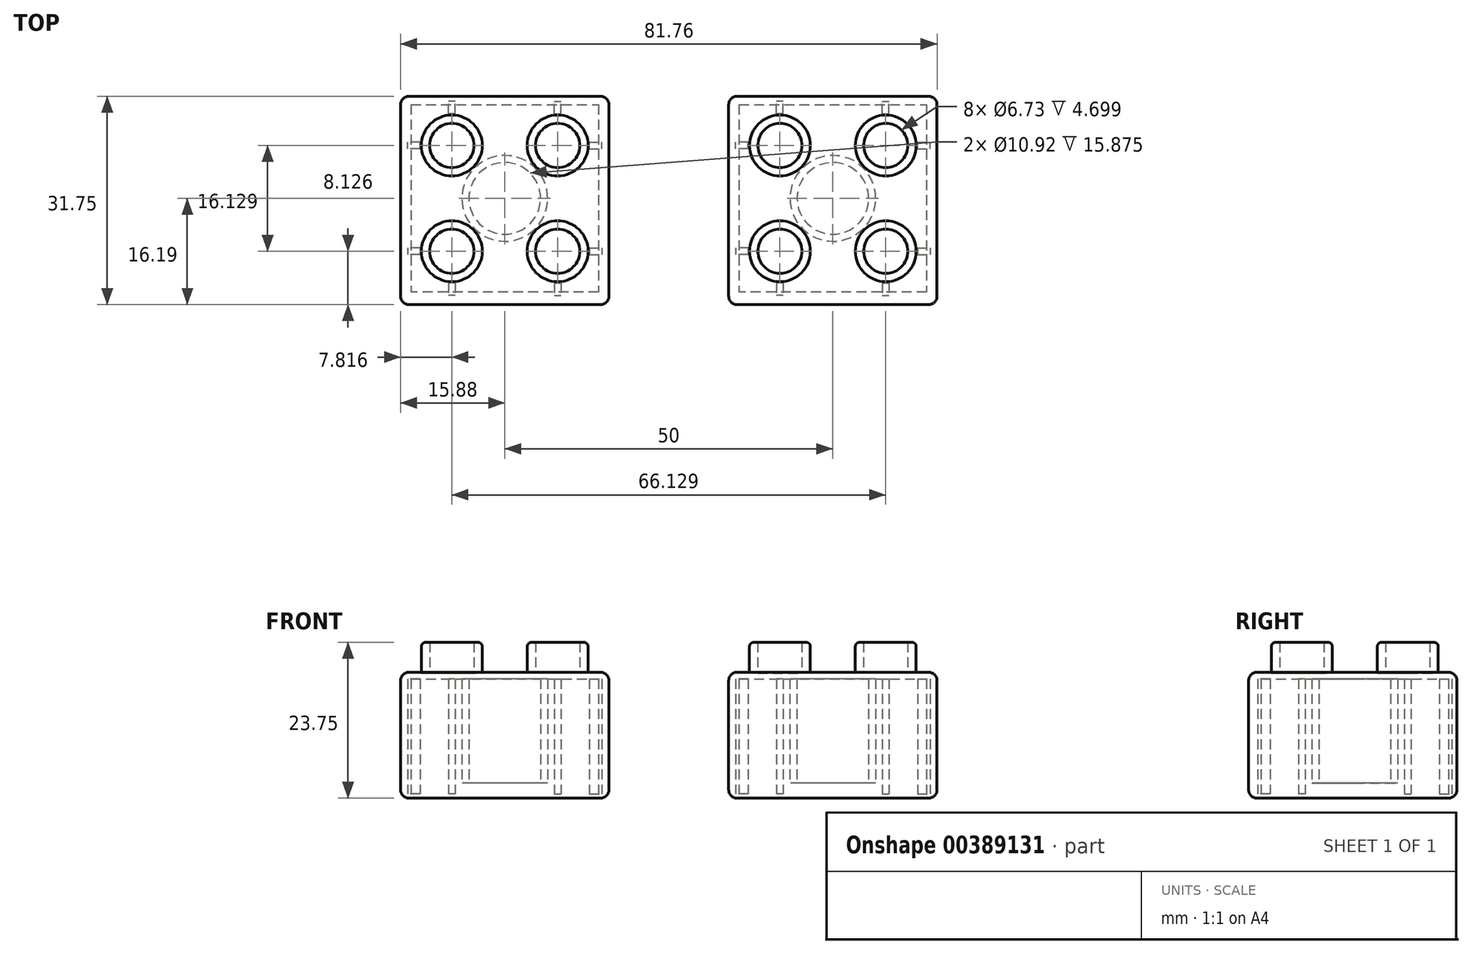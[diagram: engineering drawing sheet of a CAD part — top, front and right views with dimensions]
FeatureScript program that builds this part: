
annotation { "Feature Type Name" : "Feature", "Feature Type Description" : "" }
export const myFeature = defineFeature(function(context is Context, id is Id, definition is map)
    precondition{}
    {
        {
            var Q0;
            Q0=qCreatedBy(makeId("Top.planeOp"),FACE);
            var sketch = newSketch(context, id + "F0", { "sketchPlane" : qUnion([Q0])});
            skPoint(sketch, "E0", {"position": v(0, 16.87) * mm});
            skPoint(sketch, "E1", {"position": v(0, 15.88) * mm});
            skPoint(sketch, "E2", {"position": v(0, -14.88) * mm});
            skPoint(sketch, "E3", {"position": v(0, -15.88) * mm});
            skPoint(sketch, "E4", {"position": v(17.1, 0) * mm});
            skPoint(sketch, "E5", {"position": v(15.88, 0) * mm});
            skPoint(sketch, "E6", {"position": v(-15.88, 0) * mm});
            skPoint(sketch, "E7", {"position": v(15.64, 15.88) * mm});
            skPoint(sketch, "E8", {"position": v(15.88, 15.56) * mm});
            skPoint(sketch, "E9", {"position": v(-16.3, -15.88) * mm});
            skPoint(sketch, "E10", {"position": v(-15.88, -16.2) * mm});
            skLineSegment(sketch, "E11.bottom", {"start": v(-15.88, -16.2) * mm, "end": v(15.88, -16.2) * mm});
            skLineSegment(sketch, "E11.top", {"start": v(-15.88, 15.56) * mm, "end": v(15.88, 15.56) * mm});
            skLineSegment(sketch, "E11.left", {"start": v(-15.88, -16.2) * mm, "end": v(-15.88, 15.56) * mm});
            skLineSegment(sketch, "E11.right", {"start": v(15.88, -16.2) * mm, "end": v(15.88, 15.56) * mm});
            skSolve(sketch);
        }
        {
            var Q0;
            Q0=makeQuery(id+"F0.imprint","IMPRINT",FACE,{"disambiguationData":[TD([[makeQuery(id+"F0.imprint","IMPRINT",EDGE,{"derivedFrom":sQuery(id+"F0.wireOp",EDGE,"E11.bottom")}),1.0]])]});
            var sketch = newSketch(context, id + "F1", { "sketchPlane" : qUnion([Q0])});
            skPoint(sketch, "E12", {"position": v(14.77, 0) * mm});
            skPoint(sketch, "E13", {"position": v(14.29, 0) * mm});
            skPoint(sketch, "E14", {"position": v(-14.29, 0) * mm});
            skPoint(sketch, "E15", {"position": v(-14.29, -14.92) * mm});
            skPoint(sketch, "E16", {"position": v(-14.29, -14.29) * mm});
            skPoint(sketch, "E17", {"position": v(14.29, 14.33) * mm});
            skPoint(sketch, "E18", {"position": v(14.29, 14.29) * mm});
            skLineSegment(sketch, "E19.bottom", {"start": v(-14.29, -14.29) * mm, "end": v(14.29, -14.29) * mm});
            skLineSegment(sketch, "E19.top", {"start": v(-14.29, 14.29) * mm, "end": v(14.29, 14.29) * mm});
            skLineSegment(sketch, "E19.left", {"start": v(-14.29, -14.29) * mm, "end": v(-14.29, 14.29) * mm});
            skLineSegment(sketch, "E19.right", {"start": v(14.29, -14.29) * mm, "end": v(14.29, 14.29) * mm});
            skSolve(sketch);
        }
        {
            var Q0;
            Q0=makeQuery(id+"F1.imprint","IMPRINT",FACE,{"disambiguationData":[TD([[makeQuery(id+"F1.imprint","IMPRINT",EDGE,{"derivedFrom":sQuery(id+"F1.wireOp",EDGE,"E19.bottom")}),1.0]])]});
            var sketch = newSketch(context, id + "F2", { "sketchPlane" : qUnion([Q0])});
            skPoint(sketch, "E20", {"position": v(0, 0) * mm});
            skCircle(sketch, "E21", {"center": v(0, 0) * mm, "radius": 6.54 * mm});
            skSolve(sketch);
        }
        {
            var Q0;
            Q0=makeQuery(id+"F1.imprint","IMPRINT",FACE,{"disambiguationData":[TD([[makeQuery(id+"F1.imprint","IMPRINT",EDGE,{"derivedFrom":sQuery(id+"F1.wireOp",EDGE,"E19.bottom")}),1.0]])]});
            var sketch = newSketch(context, id + "F3", { "sketchPlane" : qUnion([Q0])});
            skPoint(sketch, "E22", {"position": v(0, 0) * mm});
            skCircle(sketch, "E23", {"center": v(0, 0) * mm, "radius": 5.46 * mm});
            skSolve(sketch);
        }
        {
            var Q0;
            Q0=makeQuery(id+"F1.imprint","IMPRINT",FACE,{"disambiguationData":[TD([[makeQuery(id+"F1.imprint","IMPRINT",EDGE,{"derivedFrom":sQuery(id+"F1.wireOp",EDGE,"E19.bottom")}),1.0]])]});
            var sketch = newSketch(context, id + "F4", { "sketchPlane" : qUnion([Q0])});
            skPoint(sketch, "E24", {"position": v(0, 1.02) * mm});
            skPoint(sketch, "E25", {"position": v(0, 0.95) * mm});
            skPoint(sketch, "E26", {"position": v(0, -0.95) * mm});
            skPoint(sketch, "E27", {"position": v(-0.23, 0) * mm});
            skPoint(sketch, "E28", {"position": v(-0.5, 0) * mm});
            skPoint(sketch, "E29", {"position": v(0.3, 0) * mm});
            skPoint(sketch, "E30", {"position": v(0.5, 0) * mm});
            skPoint(sketch, "E31", {"position": v(-0.5, -0.86) * mm});
            skPoint(sketch, "E32", {"position": v(-0.5, -0.95) * mm});
            skPoint(sketch, "E33", {"position": v(0.5, 0.95) * mm});
            skLineSegment(sketch, "E34.bottom", {"start": v(-0.5, -0.95) * mm, "end": v(0.5, -0.95) * mm});
            skLineSegment(sketch, "E34.top", {"start": v(-0.5, 0.95) * mm, "end": v(0.5, 0.95) * mm});
            skLineSegment(sketch, "E34.left", {"start": v(-0.5, -0.95) * mm, "end": v(-0.5, 0.95) * mm});
            skLineSegment(sketch, "E34.right", {"start": v(0.5, -0.95) * mm, "end": v(0.5, 0.95) * mm});
            skSolve(sketch);
        }
        {
            var Q0;
            Q0=qSketchRegion(id+"F0",true);
            extrude(context, id + "F5", {"entities" : qUnion([Q0]), "depth" : 19.18 * mm});
        }
        {
            var Q0;
            Q0=qSketchRegion(id+"F1",true);
            extrude(context, id + "F6", {"entities" : qUnion([Q0]), "operationType" : NewBodyOperationType.REMOVE, "depth" : 18.16 * mm, "hasSecondDirection" : true, "secondDirectionOppositeDirection" : true, "secondDirectionDepth" : 0.38 * mm});
        }
        {
            var Q0;
            Q0=qSketchRegion(id+"F2",true);
            extrude(context, id + "F7", {"entities" : qUnion([Q0]), "operationType" : NewBodyOperationType.ADD, "depth" : 15.88 * mm});
        }
        {
            var Q0;
            Q0=qSketchRegion(id+"F3",true);
            extrude(context, id + "F8", {"entities" : qUnion([Q0]), "operationType" : NewBodyOperationType.REMOVE, "depth" : 15.88 * mm, "hasSecondDirection" : true, "secondDirectionOppositeDirection" : true, "secondDirectionDepth" : 0.64 * mm});
        }
        {
            var Q0;
            Q0=makeQuery(id+"F7.opExtrude","SWEPT_BODY",BODY,{"disambiguationData":[OSD([sQuery(id+"F2.wireOp",EDGE,"E21")])]});
            transform(context, id + "F9", {"entities" : qUnion([Q0]), "transformType" : TransformType.TRANSLATION_3D, "dx" : 0 * mm, "dy" : 0 * mm, "dz" : 2.3 * mm, "makeCopy" : false});
        }
        {
            var Q0;
            Q0=makeQuery(id+"F4.imprint","IMPRINT",FACE,{"disambiguationData":[TD([[makeQuery(id+"F4.imprint","IMPRINT",EDGE,{"derivedFrom":sQuery(id+"F4.wireOp",EDGE,"E34.bottom")}),1.0]])]});
            extrude(context, id + "F10", {"entities" : qUnion([Q0]), "operationType" : NewBodyOperationType.ADD, "depth" : 17.53 * mm});
        }
        {
            var Q0;
            Q0=makeQuery(id+"F10.opExtrude","SWEPT_BODY",BODY,{"disambiguationData":[OSD([sQuery(id+"F4.wireOp",EDGE,"E34.bottom"),sQuery(id+"F4.wireOp",EDGE,"E34.top"),sQuery(id+"F4.wireOp",EDGE,"E34.left"),sQuery(id+"F4.wireOp",EDGE,"E34.right")])]});
            transform(context, id + "F11", {"entities" : qUnion([Q0]), "transformType" : TransformType.TRANSLATION_3D, "dx" : 8.06 * mm, "dy" : 13.86 * mm, "dz" : 0.64 * mm, "makeCopy" : false});
        }
        {
            var Q0;
            Q0=makeQuery(id+"F10.opExtrude","SWEPT_BODY",BODY,{"disambiguationData":[OSD([sQuery(id+"F4.wireOp",EDGE,"E34.bottom"),sQuery(id+"F4.wireOp",EDGE,"E34.top"),sQuery(id+"F4.wireOp",EDGE,"E34.left"),sQuery(id+"F4.wireOp",EDGE,"E34.right")])]});
            var Q1;
            Q1=qCreatedBy(makeId("Front.planeOp"),FACE);
            mirror(context, id + "F12", {"entities" : qUnion([Q0]), "mirrorPlane" : qUnion([Q1])});
        }
        {
            var Q0;
            Q0=makeQuery(id+"F12.opPattern","COPY",BODY,{"derivedFrom":makeQuery(id+"F10.opExtrude","SWEPT_BODY",BODY,{"disambiguationData":[OSD([sQuery(id+"F4.wireOp",EDGE,"E34.bottom"),sQuery(id+"F4.wireOp",EDGE,"E34.top"),sQuery(id+"F4.wireOp",EDGE,"E34.left"),sQuery(id+"F4.wireOp",EDGE,"E34.right")])]}),"instanceName":"1"});
            var Q1;
            Q1=makeQuery(id+"F10.opExtrude","SWEPT_BODY",BODY,{"disambiguationData":[OSD([sQuery(id+"F4.wireOp",EDGE,"E34.bottom"),sQuery(id+"F4.wireOp",EDGE,"E34.top"),sQuery(id+"F4.wireOp",EDGE,"E34.left"),sQuery(id+"F4.wireOp",EDGE,"E34.right")])]});
            var Q2;
            Q2=qCreatedBy(makeId("Right.planeOp"),FACE);
            mirror(context, id + "F13", {"entities" : qUnion([Q0, Q1]), "mirrorPlane" : qUnion([Q2])});
        }
        {
            var Q0;
            Q0=qCreatedBy(makeId("Front.planeOp"),FACE);
            var sketch = newSketch(context, id + "F14", { "sketchPlane" : qUnion([Q0])});
            skLineSegment(sketch, "E35", {"start": v(0, 40.9) * mm, "end": v(0, -32.36) * mm});
            skSolve(sketch);
        }
        {
            var Q0;
            Q0=makeQuery(id+"F12.opPattern","COPY",BODY,{"derivedFrom":makeQuery(id+"F10.opExtrude","SWEPT_BODY",BODY,{"disambiguationData":[OSD([sQuery(id+"F4.wireOp",EDGE,"E34.bottom"),sQuery(id+"F4.wireOp",EDGE,"E34.top"),sQuery(id+"F4.wireOp",EDGE,"E34.left"),sQuery(id+"F4.wireOp",EDGE,"E34.right")])]}),"instanceName":"1"});
            var Q1;
            Q1=makeQuery(id+"F13.opPattern","COPY",BODY,{"derivedFrom":makeQuery(id+"F12.opPattern","COPY",BODY,{"derivedFrom":makeQuery(id+"F10.opExtrude","SWEPT_BODY",BODY,{"disambiguationData":[OSD([sQuery(id+"F4.wireOp",EDGE,"E34.bottom"),sQuery(id+"F4.wireOp",EDGE,"E34.top"),sQuery(id+"F4.wireOp",EDGE,"E34.left"),sQuery(id+"F4.wireOp",EDGE,"E34.right")])]}),"instanceName":"1"}),"instanceName":"1"});
            var Q2;
            Q2=makeQuery(id+"F10.opExtrude","SWEPT_BODY",BODY,{"disambiguationData":[OSD([sQuery(id+"F4.wireOp",EDGE,"E34.bottom"),sQuery(id+"F4.wireOp",EDGE,"E34.top"),sQuery(id+"F4.wireOp",EDGE,"E34.left"),sQuery(id+"F4.wireOp",EDGE,"E34.right")])]});
            var Q3;
            Q3=makeQuery(id+"F13.opPattern","COPY",BODY,{"derivedFrom":makeQuery(id+"F10.opExtrude","SWEPT_BODY",BODY,{"disambiguationData":[OSD([sQuery(id+"F4.wireOp",EDGE,"E34.bottom"),sQuery(id+"F4.wireOp",EDGE,"E34.top"),sQuery(id+"F4.wireOp",EDGE,"E34.left"),sQuery(id+"F4.wireOp",EDGE,"E34.right")])]}),"instanceName":"1"});
            var Q4;
            Q4=sQuery(id+"F14.wireOp",EDGE,"E35");
            transform(context, id + "F15", {"entities" : qUnion([Q0, Q1, Q2, Q3]), "transformType" : TransformType.ROTATION, "transformAxis" : qUnion([Q4]), "angle" : 90 * degree, "makeCopy" : true});
        }
        {
            var Q0;
            Q0=qCreatedBy(makeId("Top.planeOp"),FACE);
            var sketch = newSketch(context, id + "F16", { "sketchPlane" : qUnion([Q0])});
            skCircle(sketch, "E36", {"center": v(0, 0) * mm, "radius": 4.64 * mm});
            skSolve(sketch);
        }
        {
            var Q0;
            Q0=qCreatedBy(makeId("Top.planeOp"),FACE);
            var sketch = newSketch(context, id + "F17", { "sketchPlane" : qUnion([Q0])});
            skCircle(sketch, "E37", {"center": v(0, 0) * mm, "radius": 3.37 * mm});
            skSolve(sketch);
        }
        {
            var Q0;
            Q0=makeQuery(id+"F16.imprint","IMPRINT",FACE,{"disambiguationData":[TD([[makeQuery(id+"F16.imprint","IMPRINT",EDGE,{"derivedFrom":sQuery(id+"F16.wireOp",EDGE,"E36")}),1.0]])]});
            extrude(context, id + "F18", {"entities" : qUnion([Q0]), "depth" : 4.7 * mm});
        }
        {
            var Q0;
            Q0=makeQuery(id+"F17.imprint","IMPRINT",FACE,{"disambiguationData":[TD([[makeQuery(id+"F17.imprint","IMPRINT",EDGE,{"derivedFrom":sQuery(id+"F17.wireOp",EDGE,"E37")}),1.0]])]});
            extrude(context, id + "F19", {"entities" : qUnion([Q0]), "operationType" : NewBodyOperationType.REMOVE, "depth" : 4.7 * mm});
        }
        {
            var Q0;
            Q0=makeQuery(id+"F18.opExtrude","SWEPT_BODY",BODY,{"disambiguationData":[OSD([sQuery(id+"F16.wireOp",EDGE,"E36")])]});
            transform(context, id + "F20", {"entities" : qUnion([Q0]), "transformType" : TransformType.TRANSLATION_3D, "dx" : 8.06 * mm, "dy" : 8.06 * mm, "dz" : 19.05 * mm, "makeCopy" : false});
        }
        {
            var Q0;
            Q0=makeQuery(id+"F18.opExtrude","SWEPT_BODY",BODY,{"disambiguationData":[OSD([sQuery(id+"F16.wireOp",EDGE,"E36")])]});
            var Q1;
            Q1=qCreatedBy(makeId("Front.planeOp"),FACE);
            mirror(context, id + "F21", {"entities" : qUnion([Q0]), "mirrorPlane" : qUnion([Q1])});
        }
        {
            var Q0;
            Q0=makeQuery(id+"F18.opExtrude","SWEPT_BODY",BODY,{"disambiguationData":[OSD([sQuery(id+"F16.wireOp",EDGE,"E36")])]});
            var Q1;
            Q1=makeQuery(id+"F21.opPattern","COPY",BODY,{"derivedFrom":makeQuery(id+"F18.opExtrude","SWEPT_BODY",BODY,{"disambiguationData":[OSD([sQuery(id+"F16.wireOp",EDGE,"E36")])]}),"instanceName":"1"});
            var Q2;
            Q2=qCreatedBy(makeId("Right.planeOp"),FACE);
            mirror(context, id + "F22", {"entities" : qUnion([Q0, Q1]), "mirrorPlane" : qUnion([Q2])});
        }
        {
            var Q0;
            Q0=makeQuery(id+"F5.opExtrude","CAP_EDGE",EDGE,{"disambiguationData":[OSD([sQuery(id+"F0.wireOp",EDGE,"E11.bottom")])],"isStart":false});
            var Q1;
            Q1=makeQuery(id+"F5.opExtrude","CAP_EDGE",EDGE,{"disambiguationData":[OSD([sQuery(id+"F0.wireOp",EDGE,"E11.left")])],"isStart":false});
            var Q2;
            Q2=makeQuery(id+"F5.opExtrude","CAP_EDGE",EDGE,{"disambiguationData":[OSD([sQuery(id+"F0.wireOp",EDGE,"E11.top")])],"isStart":false});
            var Q3;
            Q3=makeQuery(id+"F5.opExtrude","CAP_EDGE",EDGE,{"disambiguationData":[OSD([sQuery(id+"F0.wireOp",EDGE,"E11.right")])],"isStart":false});
            var Q4;
            Q4=makeQuery(id+"F5.opExtrude","SWEPT_EDGE",EDGE,{"disambiguationData":[OSD([sQuery(id+"F0.wireOp",EDGE,"E11.bottom"),sQuery(id+"F0.wireOp",EDGE,"E11.left")])]});
            var Q5;
            Q5=makeQuery(id+"F5.opExtrude","SWEPT_EDGE",EDGE,{"disambiguationData":[OSD([sQuery(id+"F0.wireOp",EDGE,"E11.bottom"),sQuery(id+"F0.wireOp",EDGE,"E11.right")])]});
            var Q6;
            Q6=makeQuery(id+"F5.opExtrude","SWEPT_EDGE",EDGE,{"disambiguationData":[OSD([sQuery(id+"F0.wireOp",EDGE,"E11.top"),sQuery(id+"F0.wireOp",EDGE,"E11.left")])]});
            var Q7;
            Q7=makeQuery(id+"F5.opExtrude","SWEPT_EDGE",EDGE,{"disambiguationData":[OSD([sQuery(id+"F0.wireOp",EDGE,"E11.top"),sQuery(id+"F0.wireOp",EDGE,"E11.right")])]});
            var Q8;
            Q8=makeQuery(id+"F5.opExtrude","CAP_EDGE",EDGE,{"disambiguationData":[OSD([sQuery(id+"F0.wireOp",EDGE,"E11.right")])],"isStart":true});
            var Q9;
            Q9=makeQuery(id+"F5.opExtrude","CAP_EDGE",EDGE,{"disambiguationData":[OSD([sQuery(id+"F0.wireOp",EDGE,"E11.bottom")])],"isStart":true});
            var Q10;
            Q10=makeQuery(id+"F5.opExtrude","CAP_EDGE",EDGE,{"disambiguationData":[OSD([sQuery(id+"F0.wireOp",EDGE,"E11.left")])],"isStart":true});
            var Q11;
            Q11=makeQuery(id+"F5.opExtrude","CAP_EDGE",EDGE,{"disambiguationData":[OSD([sQuery(id+"F0.wireOp",EDGE,"E11.top")])],"isStart":true});
            fillet(context, id + "F23", {"entities" : qUnion([Q0, Q1, Q2, Q3, Q4, Q5, Q6, Q7, Q8, Q9, Q10, Q11]), "radius" : 1.27 * mm, "tangentPropagation" : true, "allowEdgeOverflow" : false});
        }
        {
            var Q0;
            Q0=makeQuery(id+"F22.opPattern","COPY",EDGE,{"derivedFrom":makeQuery(id+"F18.opExtrude","CAP_EDGE",EDGE,{"disambiguationData":[OSD([sQuery(id+"F16.wireOp",EDGE,"E36")])],"isStart":false}),"instanceName":"1"});
            var Q1;
            Q1=makeQuery(id+"F18.opExtrude","CAP_EDGE",EDGE,{"disambiguationData":[OSD([sQuery(id+"F16.wireOp",EDGE,"E36")])],"isStart":false});
            var Q2;
            Q2=makeQuery(id+"F21.opPattern","COPY",EDGE,{"derivedFrom":makeQuery(id+"F18.opExtrude","CAP_EDGE",EDGE,{"disambiguationData":[OSD([sQuery(id+"F16.wireOp",EDGE,"E36")])],"isStart":false}),"instanceName":"1"});
            var Q3;
            Q3=makeQuery(id+"F22.opPattern","COPY",EDGE,{"derivedFrom":makeQuery(id+"F21.opPattern","COPY",EDGE,{"derivedFrom":makeQuery(id+"F18.opExtrude","CAP_EDGE",EDGE,{"disambiguationData":[OSD([sQuery(id+"F16.wireOp",EDGE,"E36")])],"isStart":false}),"instanceName":"1"}),"instanceName":"1"});
            fillet(context, id + "F24", {"entities" : qUnion([Q0, Q1, Q2, Q3]), "radius" : 0.64 * mm, "tangentPropagation" : true, "allowEdgeOverflow" : false});
        }
        {
            var Q0;
            Q0=makeQuery(id+"F13.opPattern","COPY",BODY,{"derivedFrom":makeQuery(id+"F12.opPattern","COPY",BODY,{"derivedFrom":makeQuery(id+"F10.opExtrude","SWEPT_BODY",BODY,{"disambiguationData":[OSD([sQuery(id+"F4.wireOp",EDGE,"E34.bottom"),sQuery(id+"F4.wireOp",EDGE,"E34.top"),sQuery(id+"F4.wireOp",EDGE,"E34.left"),sQuery(id+"F4.wireOp",EDGE,"E34.right")])]}),"instanceName":"1"}),"instanceName":"1"});
            var Q1;
            Q1=makeQuery(id+"F13.opPattern","COPY",BODY,{"derivedFrom":makeQuery(id+"F10.opExtrude","SWEPT_BODY",BODY,{"disambiguationData":[OSD([sQuery(id+"F4.wireOp",EDGE,"E34.bottom"),sQuery(id+"F4.wireOp",EDGE,"E34.top"),sQuery(id+"F4.wireOp",EDGE,"E34.left"),sQuery(id+"F4.wireOp",EDGE,"E34.right")])]}),"instanceName":"1"});
            var Q2;
            Q2=makeQuery(id+"F21.opPattern","COPY",BODY,{"derivedFrom":makeQuery(id+"F18.opExtrude","SWEPT_BODY",BODY,{"disambiguationData":[OSD([sQuery(id+"F16.wireOp",EDGE,"E36")])]}),"instanceName":"1"});
            var Q3;
            Q3=makeQuery(id+"F12.opPattern","COPY",BODY,{"derivedFrom":makeQuery(id+"F10.opExtrude","SWEPT_BODY",BODY,{"disambiguationData":[OSD([sQuery(id+"F4.wireOp",EDGE,"E34.bottom"),sQuery(id+"F4.wireOp",EDGE,"E34.top"),sQuery(id+"F4.wireOp",EDGE,"E34.left"),sQuery(id+"F4.wireOp",EDGE,"E34.right")])]}),"instanceName":"1"});
            var Q4;
            Q4=makeQuery(id+"F10.opExtrude","SWEPT_BODY",BODY,{"disambiguationData":[OSD([sQuery(id+"F4.wireOp",EDGE,"E34.bottom"),sQuery(id+"F4.wireOp",EDGE,"E34.top"),sQuery(id+"F4.wireOp",EDGE,"E34.left"),sQuery(id+"F4.wireOp",EDGE,"E34.right")])]});
            var Q5;
            Q5=makeQuery(id+"F18.opExtrude","SWEPT_BODY",BODY,{"disambiguationData":[OSD([sQuery(id+"F16.wireOp",EDGE,"E36")])]});
            var Q6;
            Q6=makeQuery(id+"F15.opPattern","COPY",BODY,{"derivedFrom":makeQuery(id+"F13.opPattern","COPY",BODY,{"derivedFrom":makeQuery(id+"F10.opExtrude","SWEPT_BODY",BODY,{"disambiguationData":[OSD([sQuery(id+"F4.wireOp",EDGE,"E34.bottom"),sQuery(id+"F4.wireOp",EDGE,"E34.top"),sQuery(id+"F4.wireOp",EDGE,"E34.left"),sQuery(id+"F4.wireOp",EDGE,"E34.right")])]}),"instanceName":"1"}),"instanceName":"1"});
            var Q7;
            Q7=makeQuery(id+"F22.opPattern","COPY",BODY,{"derivedFrom":makeQuery(id+"F18.opExtrude","SWEPT_BODY",BODY,{"disambiguationData":[OSD([sQuery(id+"F16.wireOp",EDGE,"E36")])]}),"instanceName":"1"});
            var Q8;
            Q8=makeQuery(id+"F15.opPattern","COPY",BODY,{"derivedFrom":makeQuery(id+"F10.opExtrude","SWEPT_BODY",BODY,{"disambiguationData":[OSD([sQuery(id+"F4.wireOp",EDGE,"E34.bottom"),sQuery(id+"F4.wireOp",EDGE,"E34.top"),sQuery(id+"F4.wireOp",EDGE,"E34.left"),sQuery(id+"F4.wireOp",EDGE,"E34.right")])]}),"instanceName":"1"});
            var Q9;
            Q9=makeQuery(id+"F5.opExtrude","SWEPT_BODY",BODY,{"disambiguationData":[OSD([sQuery(id+"F0.wireOp",EDGE,"E11.bottom"),sQuery(id+"F0.wireOp",EDGE,"E11.top"),sQuery(id+"F0.wireOp",EDGE,"E11.left"),sQuery(id+"F0.wireOp",EDGE,"E11.right")])]});
            var Q10;
            Q10=makeQuery(id+"F22.opPattern","COPY",BODY,{"derivedFrom":makeQuery(id+"F21.opPattern","COPY",BODY,{"derivedFrom":makeQuery(id+"F18.opExtrude","SWEPT_BODY",BODY,{"disambiguationData":[OSD([sQuery(id+"F16.wireOp",EDGE,"E36")])]}),"instanceName":"1"}),"instanceName":"1"});
            var Q11;
            Q11=makeQuery(id+"F15.opPattern","COPY",BODY,{"derivedFrom":makeQuery(id+"F12.opPattern","COPY",BODY,{"derivedFrom":makeQuery(id+"F10.opExtrude","SWEPT_BODY",BODY,{"disambiguationData":[OSD([sQuery(id+"F4.wireOp",EDGE,"E34.bottom"),sQuery(id+"F4.wireOp",EDGE,"E34.top"),sQuery(id+"F4.wireOp",EDGE,"E34.left"),sQuery(id+"F4.wireOp",EDGE,"E34.right")])]}),"instanceName":"1"}),"instanceName":"1"});
            var Q12;
            Q12=makeQuery(id+"F7.opExtrude","SWEPT_BODY",BODY,{"disambiguationData":[OSD([sQuery(id+"F2.wireOp",EDGE,"E21")])]});
            var Q13;
            Q13=makeQuery(id+"F15.opPattern","COPY",BODY,{"derivedFrom":makeQuery(id+"F13.opPattern","COPY",BODY,{"derivedFrom":makeQuery(id+"F12.opPattern","COPY",BODY,{"derivedFrom":makeQuery(id+"F10.opExtrude","SWEPT_BODY",BODY,{"disambiguationData":[OSD([sQuery(id+"F4.wireOp",EDGE,"E34.bottom"),sQuery(id+"F4.wireOp",EDGE,"E34.top"),sQuery(id+"F4.wireOp",EDGE,"E34.left"),sQuery(id+"F4.wireOp",EDGE,"E34.right")])]}),"instanceName":"1"}),"instanceName":"1"}),"instanceName":"1"});
            transform(context, id + "F25", {"entities" : qUnion([Q0, Q1, Q2, Q3, Q4, Q5, Q6, Q7, Q8, Q9, Q10, Q11, Q12, Q13]), "transformType" : TransformType.TRANSLATION_3D, "dx" : 50 * mm, "dy" : 0 * mm, "dz" : 0 * mm, "makeCopy" : true});
        }
    });
